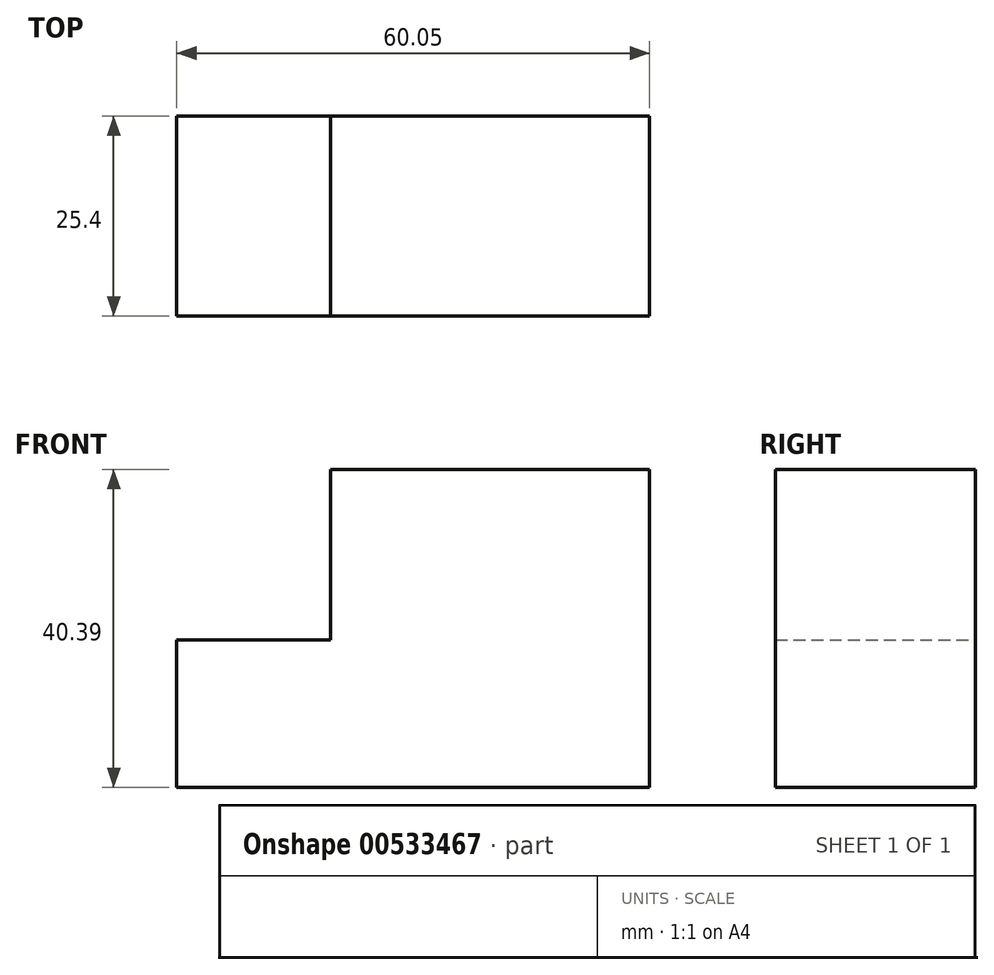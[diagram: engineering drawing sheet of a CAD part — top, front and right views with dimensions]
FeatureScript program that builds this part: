
annotation { "Feature Type Name" : "Feature", "Feature Type Description" : "" }
export const myFeature = defineFeature(function(context is Context, id is Id, definition is map)
    precondition{}
    {
        {
            var Q0;
            Q0=qCreatedBy(makeId("Front.planeOp"),FACE);
            var sketch = newSketch(context, id + "F0", { "sketchPlane" : qUnion([Q0])});
            skLineSegment(sketch, "E0", {"start": v(0, 0) * mm, "end": v(60.05, 0) * mm});
            skLineSegment(sketch, "E1", {"start": v(60.05, 0) * mm, "end": v(60.05, 40.39) * mm});
            skLineSegment(sketch, "E2", {"start": v(60.05, 40.39) * mm, "end": v(19.5, 40.39) * mm});
            skLineSegment(sketch, "E3", {"start": v(19.5, 40.39) * mm, "end": v(19.5, 18.75) * mm});
            skLineSegment(sketch, "E4", {"start": v(19.5, 18.75) * mm, "end": v(0, 18.75) * mm});
            skLineSegment(sketch, "E5", {"start": v(0, 18.75) * mm, "end": v(0, 0) * mm});
            skSolve(sketch);
        }
        {
            var Q0;
            Q0 = qSketchRegion(id + "F0", true);
            extrude(context, id + "F1", {"entities" : qUnion([Q0]), "depth" : 25.4 * mm, "offsetDistance" : 25.4 * mm});
        }
    });
